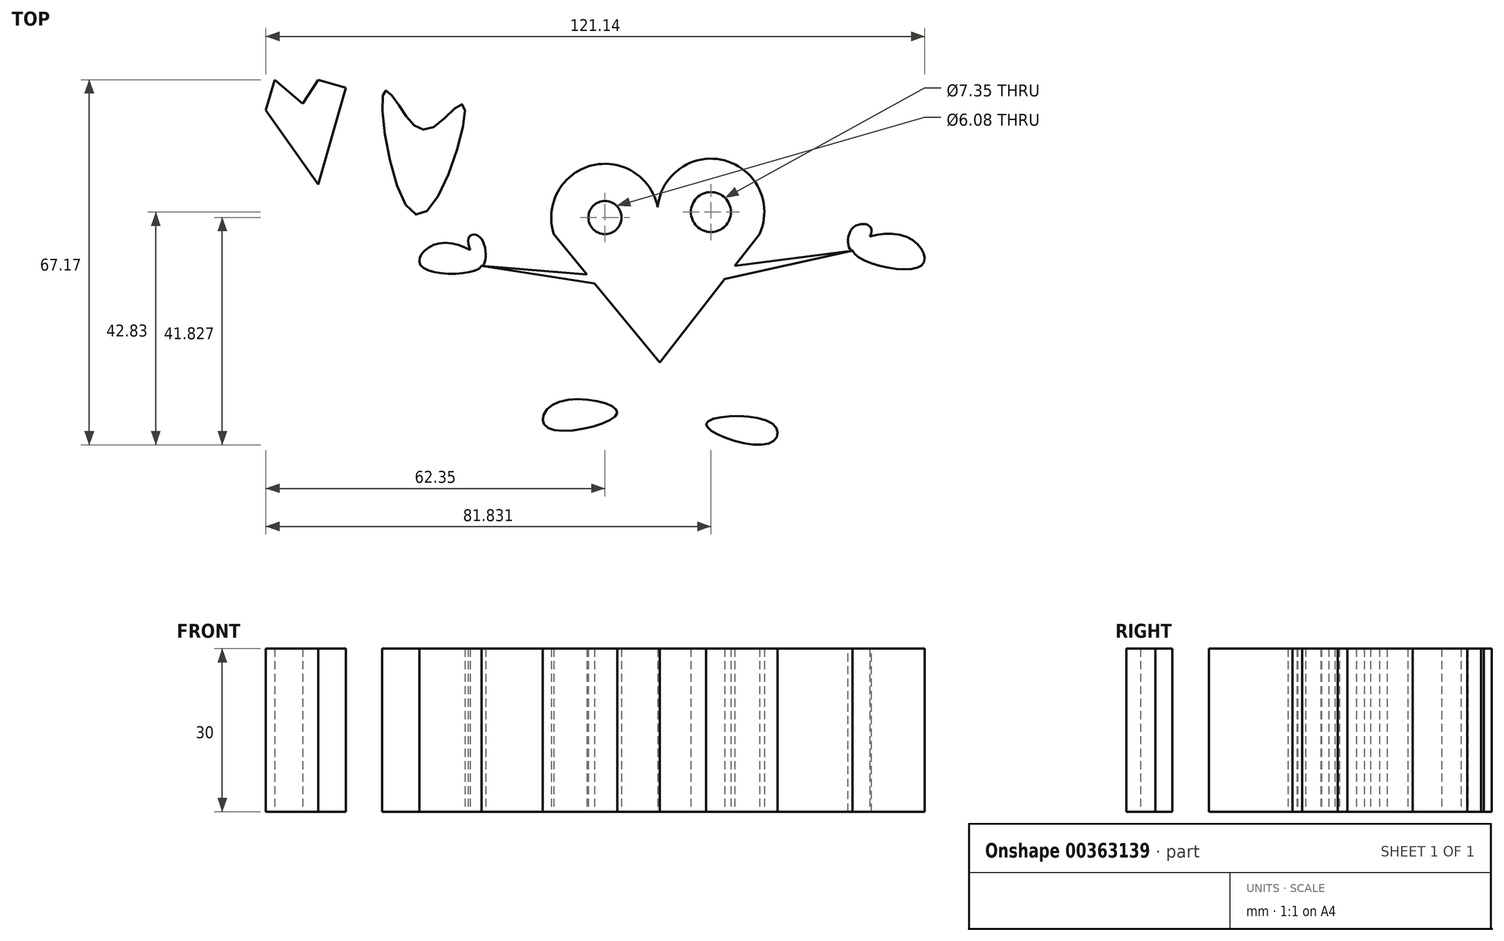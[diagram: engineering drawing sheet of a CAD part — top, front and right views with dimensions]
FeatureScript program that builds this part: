
annotation { "Feature Type Name" : "Feature", "Feature Type Description" : "" }
export const myFeature = defineFeature(function(context is Context, id is Id, definition is map)
    precondition{}
    {
        {
            var Q0;
            Q0=qCreatedBy(makeId("Top.planeOp"),FACE);
            var sketch = newSketch(context, id + "F0", { "sketchPlane" : qUnion([Q0])});
            skFitSpline(sketch, "E0", {"points": [v(-21.45, 39.99) * mm, v(-24.27, 42.43) * mm, v(-17.88, 19.85) * mm, v(-9.52, 40.05) * mm, v(-15.83, 35.67) * mm, v(-21.45, 39.99) * mm]});
            skLineSegment(sketch, "E1", {"start": v(-52.68, 31.97) * mm, "end": v(-56.56, 36.73) * mm});
            skLineSegment(sketch, "E2", {"start": v(-56.56, 36.73) * mm, "end": v(-57.97, 18.59) * mm});
            skLineSegment(sketch, "E3", {"start": v(-47.57, 28.8) * mm, "end": v(-57.97, 18.59) * mm});
            skLineSegment(sketch, "E4", {"start": v(-49.51, 28.8) * mm, "end": v(-54.99, 28.8) * mm});
            skLineSegment(sketch, "E5", {"start": v(-54.99, 27.57) * mm, "end": v(-52.68, 31.97) * mm});
            skLineSegment(sketch, "E6", {"start": v(-39.17, 40.36) * mm, "end": v(-36.26, 44.72) * mm});
            skLineSegment(sketch, "E7", {"start": v(-36.26, 44.72) * mm, "end": v(-31.18, 43.26) * mm});
            skLineSegment(sketch, "E8", {"start": v(-31.18, 43.26) * mm, "end": v(-36.26, 25.46) * mm});
            skLineSegment(sketch, "E9", {"start": v(-36.26, 25.46) * mm, "end": v(-45.9, 39.1) * mm});
            skLineSegment(sketch, "E10", {"start": v(-45.9, 39.1) * mm, "end": v(-44.27, 44.72) * mm});
            skLineSegment(sketch, "E11", {"start": v(-44.27, 44.72) * mm, "end": v(-39.17, 40.36) * mm});
            skLineSegment(sketch, "E12", {"start": v(7.04, 16.35) * mm, "end": v(26.5, -7.3) * mm});
            skLineSegment(sketch, "E13", {"start": v(26.5, -7.3) * mm, "end": v(44.88, 16.35) * mm});
            skArc(sketch, "E14", {"start": v(26.14, 21.26) * mm, "mid": v(13.98, 28.95) * mm, "end": v(7.04, 16.35) * mm});
            skArc(sketch, "E15", {"start": v(44.88, 16.35) * mm, "mid": v(38.41, 29.88) * mm, "end": v(26.14, 21.26) * mm});
            skLineSegment(sketch, "E16", {"start": v(40.3, 10.46) * mm, "end": v(61.98, 13.26) * mm});
            skLineSegment(sketch, "E17", {"start": v(61.98, 13.26) * mm, "end": v(40.3, 10.46) * mm});
            skLineSegment(sketch, "E18", {"start": v(13.15, 8.92) * mm, "end": v(-6.25, 10.46) * mm});
            skLineSegment(sketch, "E19", {"start": v(-6.25, 10.46) * mm, "end": v(13.15, 8.92) * mm});
            skLineSegment(sketch, "E20", {"start": v(23.75, -3.96) * mm, "end": v(18.68, -16.58) * mm});
            skLineSegment(sketch, "E21", {"start": v(18.68, -16.58) * mm, "end": v(23.75, -3.96) * mm});
            skLineSegment(sketch, "E22", {"start": v(29.1, -3.96) * mm, "end": v(35.05, -18.58) * mm});
            skFitSpline(sketch, "E23", {"points": [v(18.68, -16.58) * mm, v(5.94, -19.31) * mm, v(7.4, -14.76) * mm, v(18.68, -16.58) * mm]});
            skFitSpline(sketch, "E24", {"points": [v(35.05, -18.58) * mm, v(46.52, -22.22) * mm, v(47.24, -18.58) * mm, v(35.05, -18.58) * mm]});
            skFitSpline(sketch, "E25", {"points": [v(-6.25, 10.46) * mm, v(-6.25, 15.44) * mm, v(-8.61, 15.62) * mm, v(-6.25, 10.46) * mm]});
            skFitSpline(sketch, "E26", {"points": [v(-6.25, 10.46) * mm, v(-13.52, 14.71) * mm, v(-17.34, 10.46) * mm, v(-6.25, 10.46) * mm]});
            skFitSpline(sketch, "E27", {"points": [v(61.98, 13.26) * mm, v(61.98, 17.44) * mm, v(65.44, 17.26) * mm, v(61.98, 13.26) * mm]});
            skFitSpline(sketch, "E28", {"points": [v(61.98, 13.26) * mm, v(71.44, 15.99) * mm, v(74.53, 10.46) * mm, v(61.98, 13.26) * mm]});
            skCircle(sketch, "E29", {"center": v(16.44, 19.38) * mm, "radius": 3.04 * mm});
            skCircle(sketch, "E30", {"center": v(35.92, 20.38) * mm, "radius": 3.67 * mm});
            skCircle(sketch, "E31", {"center": v(16.44, 19.38) * mm, "radius": 1.36 * mm});
            skCircle(sketch, "E32", {"center": v(35.92, 20.38) * mm, "radius": 1.55 * mm});
            skArc(sketch, "E33", {"start": v(19.4, 11.8) * mm, "mid": v(21.75, 9.3) * mm, "end": v(25.05, 8.34) * mm});
            skArc(sketch, "E34", {"start": v(25.05, 8.34) * mm, "mid": v(28.2, 9.18) * mm, "end": v(30.14, 11.8) * mm});
            skLineSegment(sketch, "E35", {"start": v(-6.25, 10.46) * mm, "end": v(14.53, 7.25) * mm});
            skLineSegment(sketch, "E36", {"start": v(14.53, 7.25) * mm, "end": v(-6.25, 10.46) * mm});
            skLineSegment(sketch, "E37", {"start": v(61.98, 13.26) * mm, "end": v(38.47, 8.1) * mm});
            skLineSegment(sketch, "E38", {"start": v(38.47, 8.1) * mm, "end": v(61.98, 13.26) * mm});
            skSolve(sketch);
        }
        {
            var Q0;
            Q0 = qSketchRegion(id + "F0", true);
            extrude(context, id + "F1", {"entities" : qUnion([Q0]), "depth" : 30 * mm});
        }
    });
